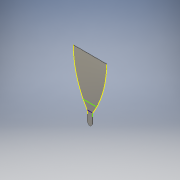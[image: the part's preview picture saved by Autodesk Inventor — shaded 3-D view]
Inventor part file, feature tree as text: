
AUTODESK INVENTOR PART (.ipt)
format: ipt  version: 2018 (Build 220112000, 112)  size: 122,880 bytes
history: native  units: in
note: dims shown in document units (in); Inventor stores cm internally (conversion verified against a paired STEP export)
features: sketch x3, extrude x1
ambient origin geometry x8: Origin, YZ Plane, XZ Plane, XY Plane, X Axis, Y Axis, Z Axis, Center Point
bodies: Solid1 (feature_tree)
feature tree (4):
  extrude  "Extrusion1"  Depth=0.4105in
  sketch  "Sketch2"  dims[d12=3.9in]
  sketch  "Sketch3"  dims[d15=0.23in d16=0.23in d17=0.028in d18=0.0in d19=2.475in d20=0.1332in]
  sketch  "Sketch1"  dims[d10=0.4105in d11=0.5in]
